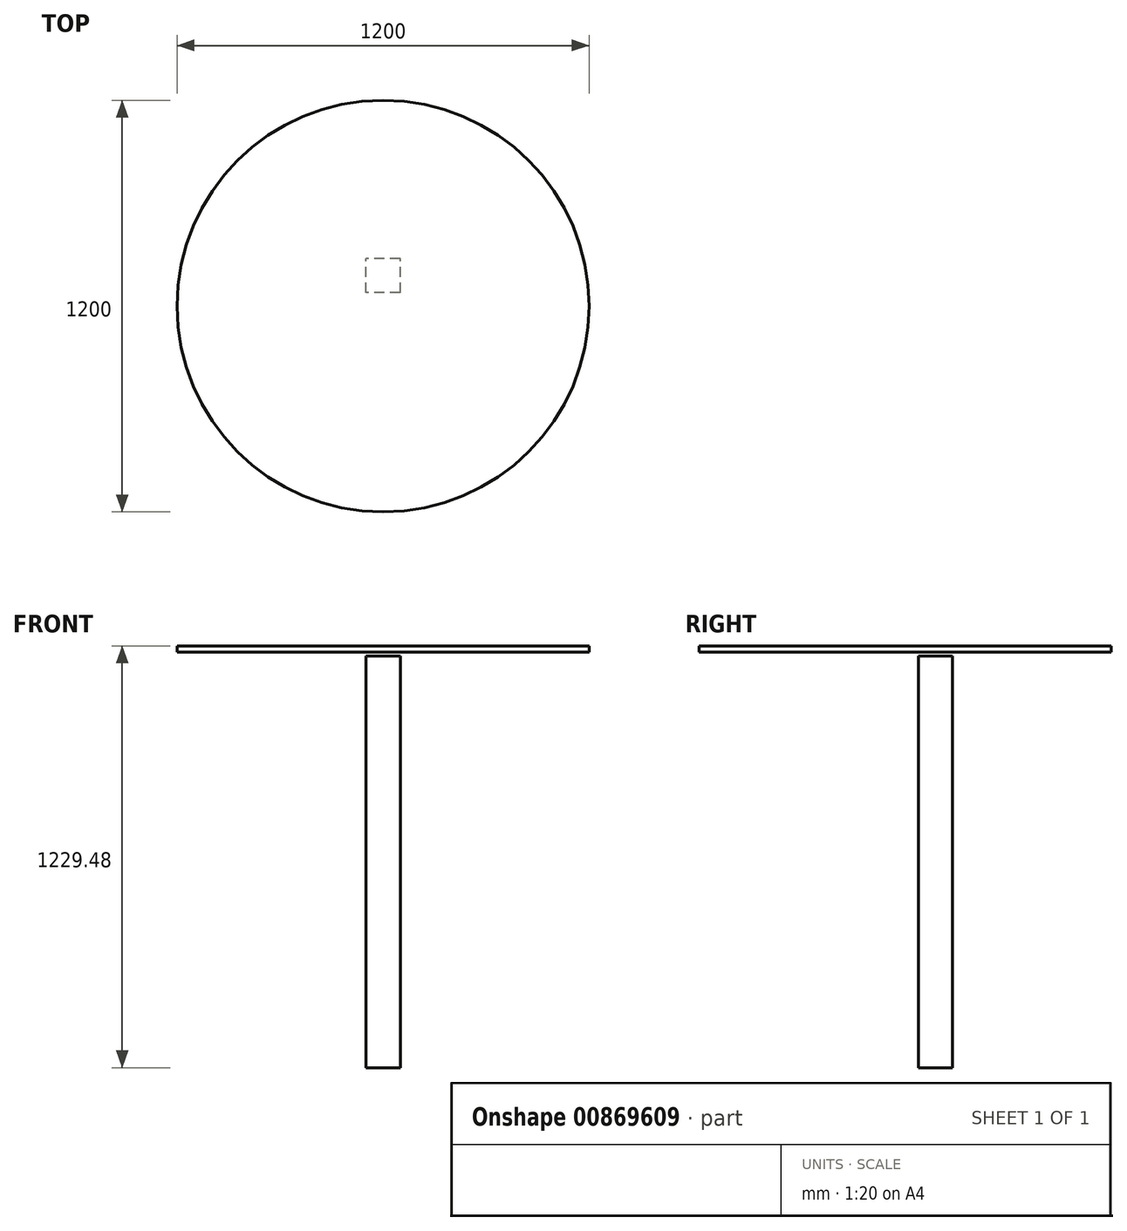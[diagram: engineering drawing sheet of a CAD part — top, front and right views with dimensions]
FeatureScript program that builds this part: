
annotation { "Feature Type Name" : "Feature", "Feature Type Description" : "" }
export const myFeature = defineFeature(function(context is Context, id is Id, definition is map)
    precondition{}
    {
        {
            var Q0;
            Q0=qCreatedBy(makeId("Top.planeOp"),FACE);
            var sketch = newSketch(context, id + "F0", { "sketchPlane" : qUnion([Q0])});
            skCircle(sketch, "E0", {"center": v(0, 0) * mm, "radius": 600 * mm});
            skSolve(sketch);
        }
        {
            var Q0;
            Q0=makeQuery(id+"F0.imprint","IMPRINT",FACE,{"disambiguationData":[TD([[makeQuery(id+"F0.imprint","IMPRINT",EDGE,{"derivedFrom":sQuery(id+"F0.wireOp",EDGE,"E0")}),1.0]])]});
            extrude(context, id + "F1", {"entities" : qUnion([Q0]), "depth" : 18 * mm, "offsetDistance" : 25 * mm});
        }
        {
            var Q0;
            Q0=qCreatedBy(makeId("Right.planeOp"),FACE);
            cPlane(context, id + "F2", {"entities" : qUnion([Q0]), "cplaneType" : CPlaneType.OFFSET, "offset" : 0 * mm, "width" : 150 * mm, "height" : 150 * mm});
        }
        {
            var Q0;
            Q0=qCreatedBy(id+"F2.planeOp",FACE);
            var sketch = newSketch(context, id + "F3", { "sketchPlane" : qUnion([Q0])});
            skLineSegment(sketch, "E1.bottom", {"start": v(38.82, -1211.48) * mm, "end": v(138.82, -1211.48) * mm});
            skLineSegment(sketch, "E1.top", {"start": v(38.82, -11.48) * mm, "end": v(138.82, -11.48) * mm});
            skLineSegment(sketch, "E1.left", {"start": v(38.82, -1211.48) * mm, "end": v(38.82, -11.48) * mm});
            skLineSegment(sketch, "E1.right", {"start": v(138.82, -1211.48) * mm, "end": v(138.82, -11.48) * mm});
            skPoint(sketch, "E2", {"position": v(38.82, -11.48) * mm});
            skSolve(sketch);
        }
        {
            var Q0;
            Q0=makeQuery(id+"F3.imprint","IMPRINT",FACE,{"disambiguationData":[TD([[makeQuery(id+"F3.imprint","IMPRINT",EDGE,{"derivedFrom":sQuery(id+"F3.wireOp",EDGE,"E1.bottom")}),1.0]])]});
            extrude(context, id + "F4", {"entities" : qUnion([Q0]), "operationType" : NewBodyOperationType.ADD, "endBound" : BoundingType.SYMMETRIC, "depth" : 100 * mm, "offsetDistance" : 25 * mm});
        }
    });
